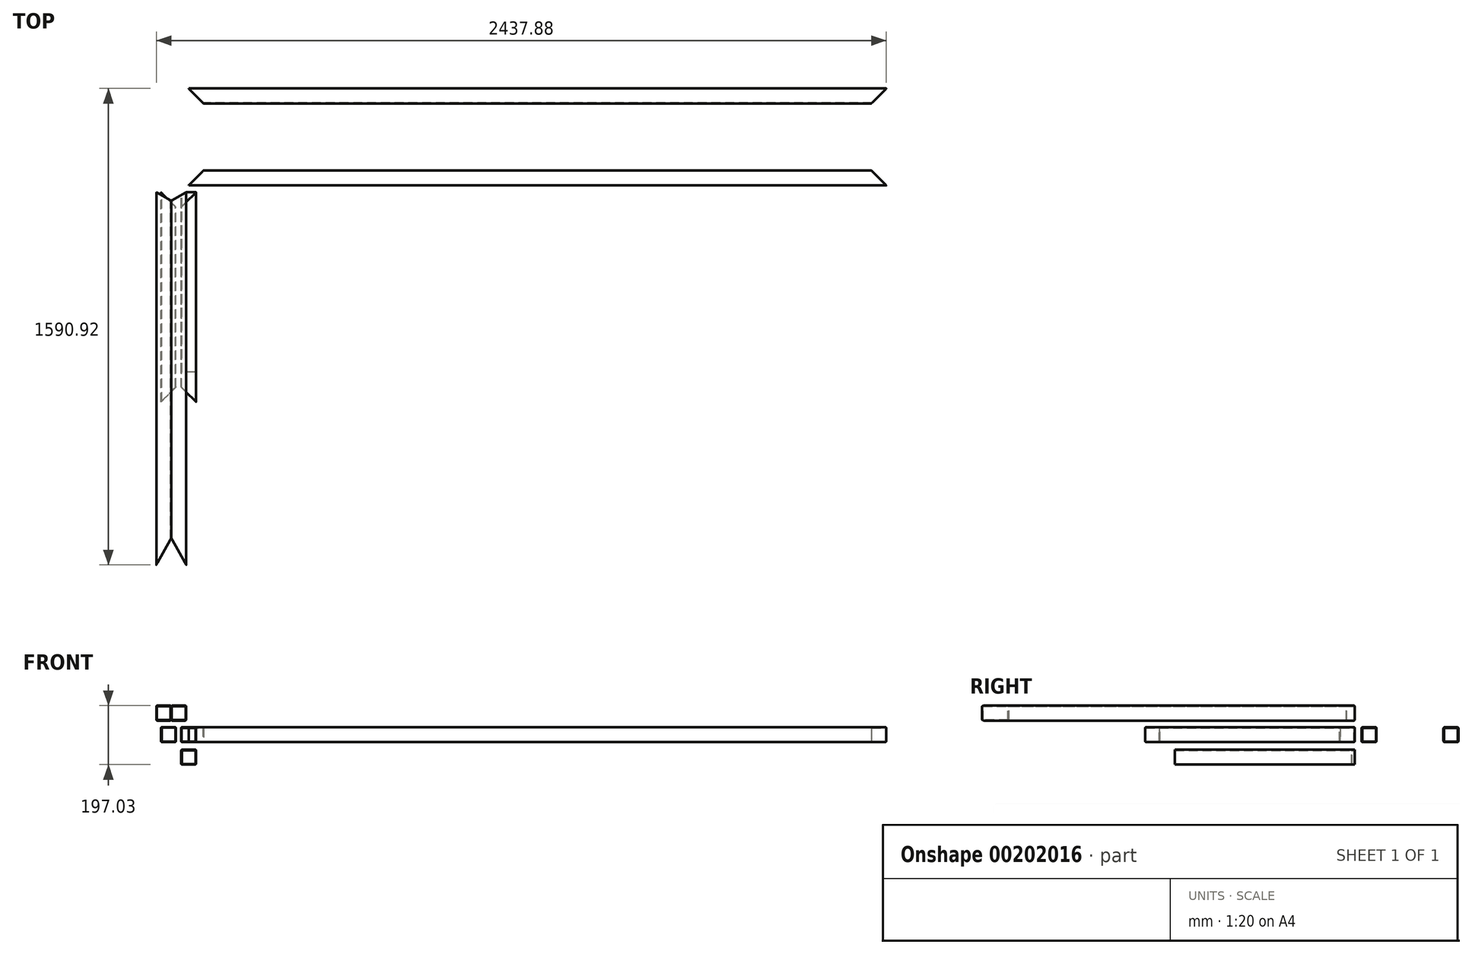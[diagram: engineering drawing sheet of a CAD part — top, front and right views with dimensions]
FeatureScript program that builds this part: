
annotation { "Feature Type Name" : "Feature", "Feature Type Description" : "" }
export const myFeature = defineFeature(function(context is Context, id is Id, definition is map)
    precondition{}
    {
        {
            var Q0;
            Q0=qCreatedBy(makeId("Front.planeOp"),FACE);
            var sketch = newSketch(context, id + "F0", { "sketchPlane" : qUnion([Q0])});
            skLineSegment(sketch, "E0.bottom", {"start": v(21, 25) * mm, "end": v(-21, 25) * mm});
            skLineSegment(sketch, "E0.top", {"start": v(21, -25) * mm, "end": v(-21, -25) * mm});
            skLineSegment(sketch, "E0.left", {"start": v(25, 21) * mm, "end": v(25, -21) * mm});
            skLineSegment(sketch, "E0.right", {"start": v(-25, 21) * mm, "end": v(-25, -21) * mm});
            skPoint(sketch, "E0.middle", {"position": v(0, 0) * mm});
            skPoint(sketch, "E1.visualSharp", {"position": v(-25, 25) * mm});
            skArc(sketch, "E1.filletArc", {"start": v(-21, 25) * mm, "mid": v(-23.83, 23.83) * mm, "end": v(-25, 21) * mm});
            skPoint(sketch, "E2.visualSharp", {"position": v(25, 25) * mm});
            skArc(sketch, "E2.filletArc", {"start": v(25, 21) * mm, "mid": v(23.83, 23.83) * mm, "end": v(21, 25) * mm});
            skPoint(sketch, "E3.visualSharp", {"position": v(25, -25) * mm});
            skArc(sketch, "E3.filletArc", {"start": v(21, -25) * mm, "mid": v(23.83, -23.83) * mm, "end": v(25, -21) * mm});
            skPoint(sketch, "E4.visualSharp", {"position": v(-25, -25) * mm});
            skArc(sketch, "E4.filletArc", {"start": v(-25, -21) * mm, "mid": v(-23.83, -23.83) * mm, "end": v(-21, -25) * mm});
            skLineSegment(sketch, "E5.0", {"start": v(-23, 23) * mm, "end": v(-23, -23) * mm});
            skLineSegment(sketch, "E5.1", {"start": v(23, 23) * mm, "end": v(-23, 23) * mm});
            skLineSegment(sketch, "E5.2", {"start": v(23, 23) * mm, "end": v(23, -23) * mm});
            skLineSegment(sketch, "E5.3", {"start": v(23, -23) * mm, "end": v(-23, -23) * mm});
            skSolve(sketch);
        }
        {
            var Q0;
            Q0=makeQuery(id+"F0.imprint","IMPRINT",FACE,{"disambiguationData":[TD([[makeQuery(id+"F0.imprint","IMPRINT",EDGE,{"derivedFrom":sQuery(id+"F0.wireOp",EDGE,"E0.bottom")}),1.0]])]});
            extrude(context, id + "F1", {"entities" : qUnion([Q0]), "depth" : 700 * mm});
        }
        {
            var Q0;
            Q0=qCreatedBy(makeId("Front.planeOp"),FACE);
            var sketch = newSketch(context, id + "F2", { "sketchPlane" : qUnion([Q0])});
            skLineSegment(sketch, "E6.bottom", {"start": v(-46.1, 25.24) * mm, "end": v(-88.1, 25.24) * mm});
            skLineSegment(sketch, "E6.top", {"start": v(-46.1, -24.76) * mm, "end": v(-88.1, -24.76) * mm});
            skLineSegment(sketch, "E6.left", {"start": v(-42.1, 21.24) * mm, "end": v(-42.1, -20.76) * mm});
            skLineSegment(sketch, "E6.right", {"start": v(-92.1, 21.24) * mm, "end": v(-92.1, -20.76) * mm});
            skPoint(sketch, "E6.middle", {"position": v(-67.1, 0.24) * mm});
            skPoint(sketch, "E7.visualSharp", {"position": v(-92.1, 25.24) * mm});
            skArc(sketch, "E7.filletArc", {"start": v(-88.1, 25.24) * mm, "mid": v(-90.93, 24.07) * mm, "end": v(-92.1, 21.24) * mm});
            skPoint(sketch, "E8.visualSharp", {"position": v(-42.1, 25.24) * mm});
            skArc(sketch, "E8.filletArc", {"start": v(-42.1, 21.24) * mm, "mid": v(-43.28, 24.07) * mm, "end": v(-46.1, 25.24) * mm});
            skPoint(sketch, "E9.visualSharp", {"position": v(-42.1, -24.76) * mm});
            skArc(sketch, "E9.filletArc", {"start": v(-46.1, -24.76) * mm, "mid": v(-43.28, -23.59) * mm, "end": v(-42.1, -20.76) * mm});
            skPoint(sketch, "E10.visualSharp", {"position": v(-92.1, -24.76) * mm});
            skArc(sketch, "E10.filletArc", {"start": v(-92.1, -20.76) * mm, "mid": v(-90.93, -23.59) * mm, "end": v(-88.1, -24.76) * mm});
            skLineSegment(sketch, "E11.0", {"start": v(-90.1, 23.24) * mm, "end": v(-90.1, -22.76) * mm});
            skLineSegment(sketch, "E11.1", {"start": v(-44.1, 23.24) * mm, "end": v(-90.1, 23.24) * mm});
            skLineSegment(sketch, "E11.2", {"start": v(-44.1, 23.24) * mm, "end": v(-44.1, -22.76) * mm});
            skLineSegment(sketch, "E11.3", {"start": v(-44.1, -22.76) * mm, "end": v(-90.1, -22.76) * mm});
            skSolve(sketch);
        }
        {
            var Q0;
            Q0=makeQuery(id+"F2.imprint","IMPRINT",FACE,{"disambiguationData":[TD([[makeQuery(id+"F2.imprint","IMPRINT",EDGE,{"derivedFrom":sQuery(id+"F2.wireOp",EDGE,"E6.bottom")}),1.0]])]});
            extrude(context, id + "F3", {"entities" : qUnion([Q0]), "depth" : 700 * mm});
        }
        {
            var Q0;
            Q0=makeQuery(id+"F1.opExtrude","SWEPT_FACE",FACE,{"disambiguationData":[OSD([sQuery(id+"F0.wireOp",EDGE,"E0.bottom")])]});
            var sketch = newSketch(context, id + "F4", { "sketchPlane" : qUnion([Q0])});
            skLineSegment(sketch, "E12.0", {"start": v(-25, -700) * mm, "end": v(-25, 0) * mm});
            skLineSegment(sketch, "E13.0", {"start": v(25, -700) * mm, "end": v(25, 0) * mm});
            skLineSegment(sketch, "E14", {"start": v(25, 0) * mm, "end": v(-25, -50) * mm});
            skLineSegment(sketch, "E15", {"start": v(25, -700) * mm, "end": v(-25, -650) * mm});
            skLineSegment(sketch, "E16", {"start": v(25, -700) * mm, "end": v(-25, -700) * mm});
            skLineSegment(sketch, "E17", {"start": v(25, 0) * mm, "end": v(-25, 0) * mm});
            skSolve(sketch);
        }
        {
            var Q0;
            {var subQ0=sQuery(id+"F4.wireOp",EDGE,"E17");var subQ1=sQuery(id+"F4.wireOp",EDGE,"E12.0");var subQ2=makeQuery(id+"F4.imprint","INTERSECT",VERTEX,{"derivedFrom":[subQ1,subQ0]});Q0=makeQuery(id+"F4.imprint","IMPRINT",FACE,{"disambiguationData":[TD([[makeQuery(id+"F4.imprint","IMPRINT",EDGE,{"disambiguationData":[TD([[subQ2,1.0]])],"derivedFrom":subQ1}),-1.0]])]});}
            var Q1;
            {var subQ0=sQuery(id+"F4.wireOp",EDGE,"E14");var subQ1=sQuery(id+"F0.wireOp",EDGE,"E0.bottom");var subQ2=makeQuery(id+"F1.opExtrude","SWEPT_EDGE",EDGE,{"disambiguationData":[OSD([subQ1,sQuery(id+"F0.wireOp",EDGE,"E2.filletArc")])]});var subQ3=makeQuery(id+"F4.imprint","INTERSECT",VERTEX,{"derivedFrom":[subQ2,subQ0]});Q1=makeQuery(id+"F4.imprint","IMPRINT",FACE,{"disambiguationData":[TD([[makeQuery(id+"F4.imprint","IMPRINT",EDGE,{"disambiguationData":[TD([[subQ3,-1.0]])],"derivedFrom":subQ0}),-1.0]])]});}
            var Q2;
            {var subQ0=sQuery(id+"F4.wireOp",EDGE,"E17");var subQ1=sQuery(id+"F4.wireOp",EDGE,"E14");var subQ2=makeQuery(id+"F4.imprint","INTERSECT",VERTEX,{"derivedFrom":[sQuery(id+"F4.wireOp",EDGE,"E13.0"),subQ1,subQ0]});Q2=makeQuery(id+"F4.imprint","IMPRINT",FACE,{"disambiguationData":[TD([[makeQuery(id+"F4.imprint","IMPRINT",EDGE,{"disambiguationData":[TD([[subQ2,-1.0]])],"derivedFrom":subQ1}),-1.0]])]});}
            var Q3;
            {var subQ0=sQuery(id+"F4.wireOp",EDGE,"E16");var subQ1=sQuery(id+"F4.wireOp",EDGE,"E12.0");var subQ2=makeQuery(id+"F4.imprint","INTERSECT",VERTEX,{"derivedFrom":[subQ1,subQ0]});Q3=makeQuery(id+"F4.imprint","IMPRINT",FACE,{"disambiguationData":[TD([[makeQuery(id+"F4.imprint","IMPRINT",EDGE,{"disambiguationData":[TD([[subQ2,-1.0]])],"derivedFrom":subQ1}),-1.0]])]});}
            var Q4;
            {var subQ0=sQuery(id+"F4.wireOp",EDGE,"E15");var subQ1=sQuery(id+"F0.wireOp",EDGE,"E0.bottom");var subQ2=makeQuery(id+"F1.opExtrude","SWEPT_EDGE",EDGE,{"disambiguationData":[OSD([subQ1,sQuery(id+"F0.wireOp",EDGE,"E2.filletArc")])]});var subQ3=makeQuery(id+"F4.imprint","INTERSECT",VERTEX,{"derivedFrom":[subQ2,subQ0]});Q4=makeQuery(id+"F4.imprint","IMPRINT",FACE,{"disambiguationData":[TD([[makeQuery(id+"F4.imprint","IMPRINT",EDGE,{"disambiguationData":[TD([[subQ3,-1.0]])],"derivedFrom":subQ0}),1.0]])]});}
            var Q5;
            {var subQ0=sQuery(id+"F4.wireOp",EDGE,"E16");var subQ1=sQuery(id+"F4.wireOp",EDGE,"E15");var subQ2=makeQuery(id+"F4.imprint","INTERSECT",VERTEX,{"derivedFrom":[sQuery(id+"F4.wireOp",EDGE,"E13.0"),subQ1,subQ0]});Q5=makeQuery(id+"F4.imprint","IMPRINT",FACE,{"disambiguationData":[TD([[makeQuery(id+"F4.imprint","IMPRINT",EDGE,{"disambiguationData":[TD([[subQ2,-1.0]])],"derivedFrom":subQ1}),1.0]])]});}
            extrude(context, id + "F5", {"entities" : qUnion([Q0, Q1, Q2, Q3, Q4, Q5]), "operationType" : NewBodyOperationType.REMOVE, "endBound" : BoundingType.THROUGH_ALL, "oppositeDirection" : true, "depth" : 25 * mm});
        }
        {
            var Q0;
            Q0=makeQuery(id+"F3.opExtrude","SWEPT_FACE",FACE,{"disambiguationData":[OSD([sQuery(id+"F2.wireOp",EDGE,"E6.bottom")])]});
            var sketch = newSketch(context, id + "F6", { "sketchPlane" : qUnion([Q0])});
            skLineSegment(sketch, "E18.0", {"start": v(-92.1, -700) * mm, "end": v(-92.1, 0) * mm});
            skLineSegment(sketch, "E19.0", {"start": v(-42.1, -700) * mm, "end": v(-42.1, 0) * mm});
            skLineSegment(sketch, "E20", {"start": v(-92.1, -700) * mm, "end": v(-42.1, -700) * mm});
            skLineSegment(sketch, "E21", {"start": v(-92.1, -700) * mm, "end": v(-42.1, -650) * mm});
            skLineSegment(sketch, "E22", {"start": v(-42.1, 0) * mm, "end": v(-92.1, 0) * mm});
            skLineSegment(sketch, "E23", {"start": v(-92.1, 0) * mm, "end": v(-42.1, -50) * mm});
            skSolve(sketch);
        }
        {
            var Q0;
            {var subQ0=sQuery(id+"F6.wireOp",EDGE,"E22");var subQ1=makeQuery(id+"F3.opExtrude","SWEPT_EDGE",EDGE,{"disambiguationData":[OSD([sQuery(id+"F2.wireOp",EDGE,"E6.bottom"),sQuery(id+"F2.wireOp",EDGE,"E7.filletArc")])]});var subQ2=makeQuery(id+"F6.imprint","INTERSECT",VERTEX,{"derivedFrom":[subQ1,subQ0]});Q0=makeQuery(id+"F6.imprint","IMPRINT",FACE,{"disambiguationData":[TD([[makeQuery(id+"F6.imprint","IMPRINT",EDGE,{"disambiguationData":[TD([[subQ2,-1.0]])],"derivedFrom":subQ0}),1.0]])]});}
            var Q1;
            {var subQ0=sQuery(id+"F6.wireOp",EDGE,"E22");var subQ1=sQuery(id+"F2.wireOp",EDGE,"E6.bottom");var subQ2=makeQuery(id+"F3.opExtrude","SWEPT_EDGE",EDGE,{"disambiguationData":[OSD([subQ1,sQuery(id+"F2.wireOp",EDGE,"E8.filletArc")])]});var subQ3=makeQuery(id+"F6.imprint","INTERSECT",VERTEX,{"derivedFrom":[subQ2,subQ0]});Q1=makeQuery(id+"F6.imprint","IMPRINT",FACE,{"disambiguationData":[TD([[makeQuery(id+"F6.imprint","IMPRINT",EDGE,{"disambiguationData":[TD([[subQ3,-1.0]])],"derivedFrom":subQ0}),1.0]])]});}
            var Q2;
            {var subQ0=sQuery(id+"F6.wireOp",EDGE,"E22");var subQ1=sQuery(id+"F6.wireOp",EDGE,"E19.0");var subQ2=makeQuery(id+"F6.imprint","INTERSECT",VERTEX,{"derivedFrom":[subQ1,subQ0]});Q2=makeQuery(id+"F6.imprint","IMPRINT",FACE,{"disambiguationData":[TD([[makeQuery(id+"F6.imprint","IMPRINT",EDGE,{"disambiguationData":[TD([[subQ2,1.0]])],"derivedFrom":subQ1}),1.0]])]});}
            var Q3;
            {var subQ0=sQuery(id+"F6.wireOp",EDGE,"E20");var subQ1=sQuery(id+"F6.wireOp",EDGE,"E19.0");var subQ2=makeQuery(id+"F6.imprint","INTERSECT",VERTEX,{"derivedFrom":[subQ1,subQ0]});Q3=makeQuery(id+"F6.imprint","IMPRINT",FACE,{"disambiguationData":[TD([[makeQuery(id+"F6.imprint","IMPRINT",EDGE,{"disambiguationData":[TD([[subQ2,-1.0]])],"derivedFrom":subQ1}),1.0]])]});}
            var Q4;
            {var subQ0=sQuery(id+"F6.wireOp",EDGE,"E20");var subQ1=sQuery(id+"F2.wireOp",EDGE,"E6.bottom");var subQ2=makeQuery(id+"F3.opExtrude","SWEPT_EDGE",EDGE,{"disambiguationData":[OSD([subQ1,sQuery(id+"F2.wireOp",EDGE,"E8.filletArc")])]});var subQ3=makeQuery(id+"F6.imprint","INTERSECT",VERTEX,{"derivedFrom":[subQ2,subQ0]});var subQ4=makeQuery(id+"F3.opExtrude","SWEPT_EDGE",EDGE,{"disambiguationData":[OSD([subQ1,sQuery(id+"F2.wireOp",EDGE,"E7.filletArc")])]});var subQ5=makeQuery(id+"F6.imprint","INTERSECT",VERTEX,{"derivedFrom":[subQ4,subQ0]});Q4=makeQuery(id+"F6.imprint","IMPRINT",FACE,{"disambiguationData":[TD([[makeQuery(id+"F6.imprint","IMPRINT",EDGE,{"disambiguationData":[TD([[subQ3,-1.0],[subQ5,1.0]])],"derivedFrom":subQ0}),-1.0]])]});}
            var Q5;
            {var subQ0=sQuery(id+"F6.wireOp",EDGE,"E20");var subQ1=makeQuery(id+"F3.opExtrude","SWEPT_EDGE",EDGE,{"disambiguationData":[OSD([sQuery(id+"F2.wireOp",EDGE,"E6.bottom"),sQuery(id+"F2.wireOp",EDGE,"E7.filletArc")])]});var subQ2=makeQuery(id+"F6.imprint","INTERSECT",VERTEX,{"derivedFrom":[subQ1,subQ0]});var subQ3=sQuery(id+"F6.wireOp",EDGE,"E21");var subQ4=makeQuery(id+"F6.imprint","INTERSECT",VERTEX,{"derivedFrom":[sQuery(id+"F6.wireOp",EDGE,"E18.0"),subQ0,subQ3]});Q5=makeQuery(id+"F6.imprint","IMPRINT",FACE,{"disambiguationData":[TD([[makeQuery(id+"F6.imprint","IMPRINT",EDGE,{"disambiguationData":[TD([[subQ2,1.0],[subQ4,-1.0]])],"derivedFrom":subQ0}),1.0]])]});}
            extrude(context, id + "F7", {"entities" : qUnion([Q0, Q1, Q2, Q3, Q4, Q5]), "operationType" : NewBodyOperationType.REMOVE, "endBound" : BoundingType.THROUGH_ALL, "oppositeDirection" : true, "depth" : 25 * mm});
        }
        {
            var Q0;
            Q0=qCreatedBy(makeId("Right.planeOp"),FACE);
            var sketch = newSketch(context, id + "F8", { "sketchPlane" : qUnion([Q0])});
            skLineSegment(sketch, "E24.bottom", {"start": v(342.69, -25) * mm, "end": v(300.69, -25) * mm});
            skLineSegment(sketch, "E24.top", {"start": v(342.69, 25) * mm, "end": v(300.69, 25) * mm});
            skLineSegment(sketch, "E24.left", {"start": v(346.69, -21) * mm, "end": v(346.69, 21) * mm});
            skLineSegment(sketch, "E24.right", {"start": v(296.69, -21) * mm, "end": v(296.69, 21) * mm});
            skPoint(sketch, "E24.middle", {"position": v(321.69, 0) * mm});
            skPoint(sketch, "E25.visualSharp", {"position": v(346.69, -25) * mm});
            skArc(sketch, "E25.filletArc", {"start": v(342.69, -25) * mm, "mid": v(345.52, -23.83) * mm, "end": v(346.69, -21) * mm});
            skPoint(sketch, "E26.visualSharp", {"position": v(296.69, -25) * mm});
            skArc(sketch, "E26.filletArc", {"start": v(296.69, -21) * mm, "mid": v(297.86, -23.83) * mm, "end": v(300.69, -25) * mm});
            skPoint(sketch, "E27.visualSharp", {"position": v(296.69, 25) * mm});
            skArc(sketch, "E27.filletArc", {"start": v(300.69, 25) * mm, "mid": v(297.86, 23.83) * mm, "end": v(296.69, 21) * mm});
            skPoint(sketch, "E28.visualSharp", {"position": v(346.69, 25) * mm});
            skArc(sketch, "E28.filletArc", {"start": v(346.69, 21) * mm, "mid": v(345.52, 23.83) * mm, "end": v(342.69, 25) * mm});
            skLineSegment(sketch, "E29.0", {"start": v(298.69, -23) * mm, "end": v(298.69, 23) * mm});
            skLineSegment(sketch, "E29.1", {"start": v(344.69, -23) * mm, "end": v(298.69, -23) * mm});
            skLineSegment(sketch, "E29.2", {"start": v(344.69, -23) * mm, "end": v(344.69, 23) * mm});
            skLineSegment(sketch, "E29.3", {"start": v(344.69, 23) * mm, "end": v(298.69, 23) * mm});
            skSolve(sketch);
        }
        {
            var Q0;
            Q0=qCreatedBy(makeId("Right.planeOp"),FACE);
            var sketch = newSketch(context, id + "F9", { "sketchPlane" : qUnion([Q0])});
            skLineSegment(sketch, "E30.bottom", {"start": v(69.15, -25) * mm, "end": v(27.15, -25) * mm});
            skLineSegment(sketch, "E30.top", {"start": v(69.15, 25) * mm, "end": v(27.15, 25) * mm});
            skLineSegment(sketch, "E30.left", {"start": v(73.15, -21) * mm, "end": v(73.15, 21) * mm});
            skLineSegment(sketch, "E30.right", {"start": v(23.15, -21) * mm, "end": v(23.15, 21) * mm});
            skPoint(sketch, "E30.middle", {"position": v(48.15, 0) * mm});
            skPoint(sketch, "E31.visualSharp", {"position": v(73.15, -25) * mm});
            skArc(sketch, "E31.filletArc", {"start": v(69.15, -25) * mm, "mid": v(71.98, -23.83) * mm, "end": v(73.15, -21) * mm});
            skPoint(sketch, "E32.visualSharp", {"position": v(23.15, -25) * mm});
            skArc(sketch, "E32.filletArc", {"start": v(23.15, -21) * mm, "mid": v(24.32, -23.83) * mm, "end": v(27.15, -25) * mm});
            skPoint(sketch, "E33.visualSharp", {"position": v(23.15, 25) * mm});
            skArc(sketch, "E33.filletArc", {"start": v(27.15, 25) * mm, "mid": v(24.32, 23.83) * mm, "end": v(23.15, 21) * mm});
            skPoint(sketch, "E34.visualSharp", {"position": v(73.15, 25) * mm});
            skArc(sketch, "E34.filletArc", {"start": v(73.15, 21) * mm, "mid": v(71.98, 23.83) * mm, "end": v(69.15, 25) * mm});
            skLineSegment(sketch, "E35.0", {"start": v(25.15, -23) * mm, "end": v(25.15, 23) * mm});
            skLineSegment(sketch, "E35.1", {"start": v(71.15, -23) * mm, "end": v(25.15, -23) * mm});
            skLineSegment(sketch, "E35.2", {"start": v(71.15, -23) * mm, "end": v(71.15, 23) * mm});
            skLineSegment(sketch, "E35.3", {"start": v(71.15, 23) * mm, "end": v(25.15, 23) * mm});
            skSolve(sketch);
        }
        {
            var Q0;
            Q0=makeQuery(id+"F8.imprint","IMPRINT",FACE,{"disambiguationData":[TD([[makeQuery(id+"F8.imprint","IMPRINT",EDGE,{"derivedFrom":sQuery(id+"F8.wireOp",EDGE,"E24.bottom")}),-1.0]])]});
            extrude(context, id + "F10", {"entities" : qUnion([Q0]), "depth" : 2330 * mm});
        }
        {
            var Q0;
            Q0=makeQuery(id+"F9.imprint","IMPRINT",FACE,{"disambiguationData":[TD([[makeQuery(id+"F9.imprint","IMPRINT",EDGE,{"derivedFrom":sQuery(id+"F9.wireOp",EDGE,"E30.bottom")}),-1.0]])]});
            extrude(context, id + "F11", {"entities" : qUnion([Q0]), "depth" : 2330 * mm});
        }
        {
            var Q0;
            Q0=makeQuery(id+"F11.opExtrude","SWEPT_FACE",FACE,{"disambiguationData":[OSD([sQuery(id+"F9.wireOp",EDGE,"E30.bottom")])]});
            var sketch = newSketch(context, id + "F12", { "sketchPlane" : qUnion([Q0])});
            skLineSegment(sketch, "E36.0", {"start": v(2330, -73.15) * mm, "end": v(0, -73.15) * mm});
            skLineSegment(sketch, "E37.0", {"start": v(2330, -23.15) * mm, "end": v(0, -23.15) * mm});
            skLineSegment(sketch, "E38", {"start": v(0, -73.15) * mm, "end": v(0, -23.15) * mm});
            skLineSegment(sketch, "E39", {"start": v(0, -23.15) * mm, "end": v(50, -73.15) * mm});
            skLineSegment(sketch, "E40", {"start": v(2330, -73.15) * mm, "end": v(2330, -23.15) * mm});
            skLineSegment(sketch, "E41", {"start": v(2280, -73.15) * mm, "end": v(2330, -23.15) * mm});
            skSolve(sketch);
        }
        {
            var Q0;
            {var subQ0=sQuery(id+"F12.wireOp",EDGE,"E40");var subQ1=sQuery(id+"F12.wireOp",EDGE,"E36.0");var subQ2=makeQuery(id+"F12.imprint","INTERSECT",VERTEX,{"derivedFrom":[subQ1,subQ0]});Q0=makeQuery(id+"F12.imprint","IMPRINT",FACE,{"disambiguationData":[TD([[makeQuery(id+"F12.imprint","IMPRINT",EDGE,{"disambiguationData":[TD([[subQ2,-1.0]])],"derivedFrom":subQ1}),-1.0]])]});}
            var Q1;
            {var subQ0=sQuery(id+"F12.wireOp",EDGE,"E40");var subQ1=sQuery(id+"F9.wireOp",EDGE,"E30.bottom");var subQ2=makeQuery(id+"F11.opExtrude","SWEPT_EDGE",EDGE,{"disambiguationData":[OSD([subQ1,sQuery(id+"F9.wireOp",EDGE,"E31.filletArc")])]});var subQ3=makeQuery(id+"F12.imprint","INTERSECT",VERTEX,{"derivedFrom":[subQ2,subQ0]});Q1=makeQuery(id+"F12.imprint","IMPRINT",FACE,{"disambiguationData":[TD([[makeQuery(id+"F12.imprint","IMPRINT",EDGE,{"disambiguationData":[TD([[subQ3,-1.0]])],"derivedFrom":subQ0}),1.0]])]});}
            var Q2;
            {var subQ0=sQuery(id+"F12.wireOp",EDGE,"E40");var subQ1=makeQuery(id+"F11.opExtrude","SWEPT_EDGE",EDGE,{"disambiguationData":[OSD([sQuery(id+"F9.wireOp",EDGE,"E30.bottom"),sQuery(id+"F9.wireOp",EDGE,"E32.filletArc")])]});var subQ2=makeQuery(id+"F12.imprint","INTERSECT",VERTEX,{"derivedFrom":[subQ1,subQ0]});Q2=makeQuery(id+"F12.imprint","IMPRINT",FACE,{"disambiguationData":[TD([[makeQuery(id+"F12.imprint","IMPRINT",EDGE,{"disambiguationData":[TD([[subQ2,-1.0]])],"derivedFrom":subQ0}),1.0]])]});}
            var Q3;
            {var subQ0=sQuery(id+"F12.wireOp",EDGE,"E38");var subQ1=sQuery(id+"F12.wireOp",EDGE,"E36.0");var subQ2=makeQuery(id+"F12.imprint","INTERSECT",VERTEX,{"derivedFrom":[subQ1,subQ0]});Q3=makeQuery(id+"F12.imprint","IMPRINT",FACE,{"disambiguationData":[TD([[makeQuery(id+"F12.imprint","IMPRINT",EDGE,{"disambiguationData":[TD([[subQ2,1.0]])],"derivedFrom":subQ1}),-1.0]])]});}
            var Q4;
            {var subQ0=sQuery(id+"F12.wireOp",EDGE,"E38");var subQ1=sQuery(id+"F9.wireOp",EDGE,"E30.bottom");var subQ2=makeQuery(id+"F11.opExtrude","SWEPT_EDGE",EDGE,{"disambiguationData":[OSD([subQ1,sQuery(id+"F9.wireOp",EDGE,"E31.filletArc")])]});var subQ3=makeQuery(id+"F12.imprint","INTERSECT",VERTEX,{"derivedFrom":[subQ2,subQ0]});Q4=makeQuery(id+"F12.imprint","IMPRINT",FACE,{"disambiguationData":[TD([[makeQuery(id+"F12.imprint","IMPRINT",EDGE,{"disambiguationData":[TD([[subQ3,-1.0]])],"derivedFrom":subQ0}),-1.0]])]});}
            var Q5;
            {var subQ0=sQuery(id+"F12.wireOp",EDGE,"E38");var subQ1=makeQuery(id+"F11.opExtrude","SWEPT_EDGE",EDGE,{"disambiguationData":[OSD([sQuery(id+"F9.wireOp",EDGE,"E30.bottom"),sQuery(id+"F9.wireOp",EDGE,"E32.filletArc")])]});var subQ2=makeQuery(id+"F12.imprint","INTERSECT",VERTEX,{"derivedFrom":[subQ1,subQ0]});Q5=makeQuery(id+"F12.imprint","IMPRINT",FACE,{"disambiguationData":[TD([[makeQuery(id+"F12.imprint","IMPRINT",EDGE,{"disambiguationData":[TD([[subQ2,-1.0]])],"derivedFrom":subQ0}),-1.0]])]});}
            extrude(context, id + "F13", {"entities" : qUnion([Q0, Q1, Q2, Q3, Q4, Q5]), "operationType" : NewBodyOperationType.REMOVE, "endBound" : BoundingType.THROUGH_ALL, "oppositeDirection" : true, "depth" : 25 * mm});
        }
        {
            var Q0;
            Q0=makeQuery(id+"F10.opExtrude","SWEPT_FACE",FACE,{"disambiguationData":[OSD([sQuery(id+"F8.wireOp",EDGE,"E24.bottom")])]});
            var sketch = newSketch(context, id + "F14", { "sketchPlane" : qUnion([Q0])});
            skLineSegment(sketch, "E42.0", {"start": v(2330, -346.69) * mm, "end": v(0, -346.69) * mm});
            skLineSegment(sketch, "E43.0", {"start": v(2330, -296.69) * mm, "end": v(0, -296.69) * mm});
            skLineSegment(sketch, "E44", {"start": v(0, -296.69) * mm, "end": v(0, -346.69) * mm});
            skLineSegment(sketch, "E45", {"start": v(50, -296.69) * mm, "end": v(0, -346.69) * mm});
            skLineSegment(sketch, "E46", {"start": v(2330, -296.69) * mm, "end": v(2330, -346.69) * mm});
            skLineSegment(sketch, "E47", {"start": v(2330, -346.69) * mm, "end": v(2280, -296.69) * mm});
            skSolve(sketch);
        }
        {
            var Q0;
            {var subQ0=sQuery(id+"F14.wireOp",EDGE,"E46");var subQ1=makeQuery(id+"F10.opExtrude","SWEPT_EDGE",EDGE,{"disambiguationData":[OSD([sQuery(id+"F8.wireOp",EDGE,"E24.bottom"),sQuery(id+"F8.wireOp",EDGE,"E25.filletArc")])]});var subQ2=makeQuery(id+"F14.imprint","INTERSECT",VERTEX,{"derivedFrom":[subQ1,subQ0]});var subQ3=sQuery(id+"F14.wireOp",EDGE,"E47");var subQ4=makeQuery(id+"F14.imprint","INTERSECT",VERTEX,{"derivedFrom":[sQuery(id+"F14.wireOp",EDGE,"E42.0"),subQ0,subQ3]});Q0=makeQuery(id+"F14.imprint","IMPRINT",FACE,{"disambiguationData":[TD([[makeQuery(id+"F14.imprint","IMPRINT",EDGE,{"disambiguationData":[TD([[subQ2,-1.0],[subQ4,1.0]])],"derivedFrom":subQ0}),-1.0]])]});}
            var Q1;
            {var subQ0=sQuery(id+"F14.wireOp",EDGE,"E46");var subQ1=sQuery(id+"F8.wireOp",EDGE,"E24.bottom");var subQ2=makeQuery(id+"F10.opExtrude","SWEPT_EDGE",EDGE,{"disambiguationData":[OSD([subQ1,sQuery(id+"F8.wireOp",EDGE,"E25.filletArc")])]});var subQ3=makeQuery(id+"F14.imprint","INTERSECT",VERTEX,{"derivedFrom":[subQ2,subQ0]});var subQ4=makeQuery(id+"F10.opExtrude","SWEPT_EDGE",EDGE,{"disambiguationData":[OSD([subQ1,sQuery(id+"F8.wireOp",EDGE,"E26.filletArc")])]});var subQ5=makeQuery(id+"F14.imprint","INTERSECT",VERTEX,{"derivedFrom":[subQ4,subQ0]});Q1=makeQuery(id+"F14.imprint","IMPRINT",FACE,{"disambiguationData":[TD([[makeQuery(id+"F14.imprint","IMPRINT",EDGE,{"disambiguationData":[TD([[subQ3,-1.0],[subQ5,1.0]])],"derivedFrom":subQ0}),1.0]])]});}
            var Q2;
            {var subQ0=sQuery(id+"F14.wireOp",EDGE,"E46");var subQ1=sQuery(id+"F14.wireOp",EDGE,"E43.0");var subQ2=makeQuery(id+"F14.imprint","INTERSECT",VERTEX,{"derivedFrom":[subQ1,subQ0]});Q2=makeQuery(id+"F14.imprint","IMPRINT",FACE,{"disambiguationData":[TD([[makeQuery(id+"F14.imprint","IMPRINT",EDGE,{"disambiguationData":[TD([[subQ2,-1.0]])],"derivedFrom":subQ1}),1.0]])]});}
            var Q3;
            {var subQ0=sQuery(id+"F14.wireOp",EDGE,"E44");var subQ1=sQuery(id+"F14.wireOp",EDGE,"E43.0");var subQ2=makeQuery(id+"F14.imprint","INTERSECT",VERTEX,{"derivedFrom":[subQ1,subQ0]});Q3=makeQuery(id+"F14.imprint","IMPRINT",FACE,{"disambiguationData":[TD([[makeQuery(id+"F14.imprint","IMPRINT",EDGE,{"disambiguationData":[TD([[subQ2,1.0]])],"derivedFrom":subQ1}),1.0]])]});}
            var Q4;
            {var subQ0=sQuery(id+"F14.wireOp",EDGE,"E44");var subQ1=sQuery(id+"F8.wireOp",EDGE,"E24.bottom");var subQ2=makeQuery(id+"F10.opExtrude","SWEPT_EDGE",EDGE,{"disambiguationData":[OSD([subQ1,sQuery(id+"F8.wireOp",EDGE,"E25.filletArc")])]});var subQ3=makeQuery(id+"F14.imprint","INTERSECT",VERTEX,{"derivedFrom":[subQ2,subQ0]});var subQ4=makeQuery(id+"F10.opExtrude","SWEPT_EDGE",EDGE,{"disambiguationData":[OSD([subQ1,sQuery(id+"F8.wireOp",EDGE,"E26.filletArc")])]});var subQ5=makeQuery(id+"F14.imprint","INTERSECT",VERTEX,{"derivedFrom":[subQ4,subQ0]});Q4=makeQuery(id+"F14.imprint","IMPRINT",FACE,{"disambiguationData":[TD([[makeQuery(id+"F14.imprint","IMPRINT",EDGE,{"disambiguationData":[TD([[subQ3,-1.0],[subQ5,1.0]])],"derivedFrom":subQ0}),-1.0]])]});}
            var Q5;
            {var subQ0=sQuery(id+"F14.wireOp",EDGE,"E44");var subQ1=makeQuery(id+"F10.opExtrude","SWEPT_EDGE",EDGE,{"disambiguationData":[OSD([sQuery(id+"F8.wireOp",EDGE,"E24.bottom"),sQuery(id+"F8.wireOp",EDGE,"E25.filletArc")])]});var subQ2=makeQuery(id+"F14.imprint","INTERSECT",VERTEX,{"derivedFrom":[subQ1,subQ0]});var subQ3=sQuery(id+"F14.wireOp",EDGE,"E45");var subQ4=makeQuery(id+"F14.imprint","INTERSECT",VERTEX,{"derivedFrom":[sQuery(id+"F14.wireOp",EDGE,"E42.0"),subQ0,subQ3]});Q5=makeQuery(id+"F14.imprint","IMPRINT",FACE,{"disambiguationData":[TD([[makeQuery(id+"F14.imprint","IMPRINT",EDGE,{"disambiguationData":[TD([[subQ2,-1.0],[subQ4,1.0]])],"derivedFrom":subQ0}),1.0]])]});}
            extrude(context, id + "F15", {"entities" : qUnion([Q0, Q1, Q2, Q3, Q4, Q5]), "operationType" : NewBodyOperationType.REMOVE, "endBound" : BoundingType.THROUGH_ALL, "oppositeDirection" : true, "depth" : 25 * mm});
        }
        {
            var Q0;
            Q0=qCreatedBy(makeId("Front.planeOp"),FACE);
            var sketch = newSketch(context, id + "F16", { "sketchPlane" : qUnion([Q0])});
            skLineSegment(sketch, "E48.bottom", {"start": v(21.25, -49.95) * mm, "end": v(-20.75, -49.95) * mm});
            skLineSegment(sketch, "E48.top", {"start": v(21.25, -99.95) * mm, "end": v(-20.75, -99.95) * mm});
            skLineSegment(sketch, "E48.left", {"start": v(25.25, -53.95) * mm, "end": v(25.25, -95.95) * mm});
            skLineSegment(sketch, "E48.right", {"start": v(-24.75, -53.95) * mm, "end": v(-24.75, -95.95) * mm});
            skPoint(sketch, "E48.middle", {"position": v(0.25, -74.95) * mm});
            skPoint(sketch, "E49.visualSharp", {"position": v(-24.75, -49.95) * mm});
            skArc(sketch, "E49.filletArc", {"start": v(-20.75, -49.95) * mm, "mid": v(-23.58, -51.13) * mm, "end": v(-24.75, -53.95) * mm});
            skPoint(sketch, "E50.visualSharp", {"position": v(25.25, -49.95) * mm});
            skArc(sketch, "E50.filletArc", {"start": v(25.25, -53.95) * mm, "mid": v(24.08, -51.13) * mm, "end": v(21.25, -49.95) * mm});
            skPoint(sketch, "E51.visualSharp", {"position": v(25.25, -99.95) * mm});
            skArc(sketch, "E51.filletArc", {"start": v(21.25, -99.95) * mm, "mid": v(24.08, -98.78) * mm, "end": v(25.25, -95.95) * mm});
            skPoint(sketch, "E52.visualSharp", {"position": v(-24.75, -99.95) * mm});
            skArc(sketch, "E52.filletArc", {"start": v(-24.75, -95.95) * mm, "mid": v(-23.58, -98.78) * mm, "end": v(-20.75, -99.95) * mm});
            skLineSegment(sketch, "E53.0", {"start": v(-22.75, -51.95) * mm, "end": v(-22.75, -97.95) * mm});
            skLineSegment(sketch, "E53.1", {"start": v(23.25, -51.95) * mm, "end": v(-22.75, -51.95) * mm});
            skLineSegment(sketch, "E53.2", {"start": v(23.25, -51.95) * mm, "end": v(23.25, -97.95) * mm});
            skLineSegment(sketch, "E53.3", {"start": v(23.25, -97.95) * mm, "end": v(-22.75, -97.95) * mm});
            skSolve(sketch);
        }
        {
            var Q0;
            Q0=makeQuery(id+"F16.imprint","IMPRINT",FACE,{"disambiguationData":[TD([[makeQuery(id+"F16.imprint","IMPRINT",EDGE,{"derivedFrom":sQuery(id+"F16.wireOp",EDGE,"E48.bottom")}),1.0]])]});
            extrude(context, id + "F17", {"entities" : qUnion([Q0]), "depth" : 600 * mm});
        }
        {
            var Q0;
            Q0=qCreatedBy(makeId("Front.planeOp"),FACE);
            var sketch = newSketch(context, id + "F18", { "sketchPlane" : qUnion([Q0])});
            skLineSegment(sketch, "E54.bottom", {"start": v(60.67, 97.08) * mm, "end": v(18.67, 97.08) * mm});
            skLineSegment(sketch, "E54.top", {"start": v(60.67, 47.08) * mm, "end": v(18.67, 47.08) * mm});
            skLineSegment(sketch, "E54.left", {"start": v(64.67, 93.08) * mm, "end": v(64.67, 51.08) * mm});
            skLineSegment(sketch, "E54.right", {"start": v(14.67, 93.08) * mm, "end": v(14.67, 51.08) * mm});
            skPoint(sketch, "E54.middle", {"position": v(39.67, 72.08) * mm});
            skPoint(sketch, "E55.visualSharp", {"position": v(14.67, 97.08) * mm});
            skArc(sketch, "E55.filletArc", {"start": v(18.67, 97.08) * mm, "mid": v(15.84, 95.91) * mm, "end": v(14.67, 93.08) * mm});
            skPoint(sketch, "E56.visualSharp", {"position": v(64.67, 97.08) * mm});
            skArc(sketch, "E56.filletArc", {"start": v(64.67, 93.08) * mm, "mid": v(63.5, 95.91) * mm, "end": v(60.67, 97.08) * mm});
            skPoint(sketch, "E57.visualSharp", {"position": v(64.67, 47.08) * mm});
            skArc(sketch, "E57.filletArc", {"start": v(60.67, 47.08) * mm, "mid": v(63.5, 48.25) * mm, "end": v(64.67, 51.08) * mm});
            skPoint(sketch, "E58.visualSharp", {"position": v(14.67, 47.08) * mm});
            skArc(sketch, "E58.filletArc", {"start": v(14.67, 51.08) * mm, "mid": v(15.84, 48.25) * mm, "end": v(18.67, 47.08) * mm});
            skLineSegment(sketch, "E59.0", {"start": v(16.67, 95.08) * mm, "end": v(16.67, 49.08) * mm});
            skLineSegment(sketch, "E59.1", {"start": v(62.67, 95.08) * mm, "end": v(16.67, 95.08) * mm});
            skLineSegment(sketch, "E59.2", {"start": v(62.67, 95.08) * mm, "end": v(62.67, 49.08) * mm});
            skLineSegment(sketch, "E59.3", {"start": v(62.67, 49.08) * mm, "end": v(16.67, 49.08) * mm});
            skSolve(sketch);
        }
        {
            var Q0;
            Q0=qCreatedBy(makeId("Front.planeOp"),FACE);
            var sketch = newSketch(context, id + "F19", { "sketchPlane" : qUnion([Q0])});
            skLineSegment(sketch, "E60.bottom", {"start": v(-11.88, 97.08) * mm, "end": v(-53.88, 97.08) * mm});
            skLineSegment(sketch, "E60.top", {"start": v(-11.88, 47.08) * mm, "end": v(-53.88, 47.08) * mm});
            skLineSegment(sketch, "E60.left", {"start": v(-7.88, 93.08) * mm, "end": v(-7.88, 51.08) * mm});
            skLineSegment(sketch, "E60.right", {"start": v(-57.88, 93.08) * mm, "end": v(-57.88, 51.08) * mm});
            skPoint(sketch, "E60.middle", {"position": v(-32.88, 72.08) * mm});
            skPoint(sketch, "E61.visualSharp", {"position": v(-57.88, 97.08) * mm});
            skArc(sketch, "E61.filletArc", {"start": v(-53.88, 97.08) * mm, "mid": v(-56.7, 95.91) * mm, "end": v(-57.88, 93.08) * mm});
            skPoint(sketch, "E62.visualSharp", {"position": v(-7.88, 97.08) * mm});
            skArc(sketch, "E62.filletArc", {"start": v(-7.88, 93.08) * mm, "mid": v(-9.05, 95.91) * mm, "end": v(-11.88, 97.08) * mm});
            skPoint(sketch, "E63.visualSharp", {"position": v(-7.88, 47.08) * mm});
            skArc(sketch, "E63.filletArc", {"start": v(-11.88, 47.08) * mm, "mid": v(-9.05, 48.25) * mm, "end": v(-7.88, 51.08) * mm});
            skPoint(sketch, "E64.visualSharp", {"position": v(-57.88, 47.08) * mm});
            skArc(sketch, "E64.filletArc", {"start": v(-57.88, 51.08) * mm, "mid": v(-56.7, 48.25) * mm, "end": v(-53.88, 47.08) * mm});
            skLineSegment(sketch, "E65.0", {"start": v(-55.88, 95.08) * mm, "end": v(-55.88, 49.08) * mm});
            skLineSegment(sketch, "E65.1", {"start": v(-9.88, 95.08) * mm, "end": v(-55.88, 95.08) * mm});
            skLineSegment(sketch, "E65.2", {"start": v(-9.88, 95.08) * mm, "end": v(-9.88, 49.08) * mm});
            skLineSegment(sketch, "E65.3", {"start": v(-9.88, 49.08) * mm, "end": v(-55.88, 49.08) * mm});
            skSolve(sketch);
        }
        {
            var Q0;
            Q0=makeQuery(id+"F18.imprint","IMPRINT",FACE,{"disambiguationData":[TD([[makeQuery(id+"F18.imprint","IMPRINT",EDGE,{"derivedFrom":sQuery(id+"F18.wireOp",EDGE,"E54.bottom")}),1.0]])]});
            extrude(context, id + "F20", {"entities" : qUnion([Q0]), "depth" : 1244.23 * mm});
        }
        {
            var Q0;
            Q0=makeQuery(id+"F19.imprint","IMPRINT",FACE,{"disambiguationData":[TD([[makeQuery(id+"F19.imprint","IMPRINT",EDGE,{"derivedFrom":sQuery(id+"F19.wireOp",EDGE,"E60.bottom")}),1.0]])]});
            extrude(context, id + "F21", {"entities" : qUnion([Q0]), "depth" : 1244.23 * mm});
        }
        {
            var Q0;
            Q0=makeQuery(id+"F21.opExtrude","SWEPT_FACE",FACE,{"disambiguationData":[OSD([sQuery(id+"F19.wireOp",EDGE,"E60.bottom")])]});
            var sketch = newSketch(context, id + "F22", { "sketchPlane" : qUnion([Q0])});
            skLineSegment(sketch, "E66.0", {"start": v(-57.88, -1244.23) * mm, "end": v(-57.88, 0) * mm});
            skLineSegment(sketch, "E67.0", {"start": v(-7.88, -1244.23) * mm, "end": v(-7.88, 0) * mm});
            skLineSegment(sketch, "E68", {"start": v(-57.88, 0) * mm, "end": v(-7.88, 0) * mm});
            skLineSegment(sketch, "E69", {"start": v(-7.88, 0) * mm, "end": v(-57.88, -27.72) * mm});
            skLineSegment(sketch, "E70", {"start": v(-57.88, -1244.23) * mm, "end": v(-7.88, -1244.23) * mm});
            skLineSegment(sketch, "E71", {"start": v(-7.88, -1244.23) * mm, "end": v(-57.88, -1154.02) * mm});
            skSolve(sketch);
        }
        {
            var Q0;
            {var subQ0=sQuery(id+"F22.wireOp",EDGE,"E70");var subQ1=sQuery(id+"F22.wireOp",EDGE,"E66.0");var subQ2=makeQuery(id+"F22.imprint","INTERSECT",VERTEX,{"derivedFrom":[subQ1,subQ0]});Q0=makeQuery(id+"F22.imprint","IMPRINT",FACE,{"disambiguationData":[TD([[makeQuery(id+"F22.imprint","IMPRINT",EDGE,{"disambiguationData":[TD([[subQ2,-1.0]])],"derivedFrom":subQ1}),-1.0]])]});}
            var Q1;
            {var subQ0=sQuery(id+"F22.wireOp",EDGE,"E70");var subQ1=sQuery(id+"F19.wireOp",EDGE,"E60.bottom");var subQ2=makeQuery(id+"F21.opExtrude","SWEPT_EDGE",EDGE,{"disambiguationData":[OSD([subQ1,sQuery(id+"F19.wireOp",EDGE,"E62.filletArc")])]});var subQ3=makeQuery(id+"F22.imprint","INTERSECT",VERTEX,{"derivedFrom":[subQ2,subQ0]});var subQ4=makeQuery(id+"F21.opExtrude","SWEPT_EDGE",EDGE,{"disambiguationData":[OSD([subQ1,sQuery(id+"F19.wireOp",EDGE,"E61.filletArc")])]});var subQ5=makeQuery(id+"F22.imprint","INTERSECT",VERTEX,{"derivedFrom":[subQ4,subQ0]});Q1=makeQuery(id+"F22.imprint","IMPRINT",FACE,{"disambiguationData":[TD([[makeQuery(id+"F22.imprint","IMPRINT",EDGE,{"disambiguationData":[TD([[subQ3,-1.0],[subQ5,1.0]])],"derivedFrom":subQ0}),-1.0]])]});}
            var Q2;
            {var subQ0=sQuery(id+"F22.wireOp",EDGE,"E70");var subQ1=makeQuery(id+"F21.opExtrude","SWEPT_EDGE",EDGE,{"disambiguationData":[OSD([sQuery(id+"F19.wireOp",EDGE,"E60.bottom"),sQuery(id+"F19.wireOp",EDGE,"E62.filletArc")])]});var subQ2=makeQuery(id+"F22.imprint","INTERSECT",VERTEX,{"derivedFrom":[subQ1,subQ0]});var subQ3=sQuery(id+"F22.wireOp",EDGE,"E71");var subQ4=makeQuery(id+"F22.imprint","INTERSECT",VERTEX,{"derivedFrom":[sQuery(id+"F22.wireOp",EDGE,"E67.0"),subQ0,subQ3]});Q2=makeQuery(id+"F22.imprint","IMPRINT",FACE,{"disambiguationData":[TD([[makeQuery(id+"F22.imprint","IMPRINT",EDGE,{"disambiguationData":[TD([[subQ2,-1.0],[subQ4,1.0]])],"derivedFrom":subQ0}),1.0]])]});}
            var Q3;
            {var subQ0=sQuery(id+"F22.wireOp",EDGE,"E68");var subQ1=sQuery(id+"F22.wireOp",EDGE,"E66.0");var subQ2=makeQuery(id+"F22.imprint","INTERSECT",VERTEX,{"derivedFrom":[subQ1,subQ0]});Q3=makeQuery(id+"F22.imprint","IMPRINT",FACE,{"disambiguationData":[TD([[makeQuery(id+"F22.imprint","IMPRINT",EDGE,{"disambiguationData":[TD([[subQ2,1.0]])],"derivedFrom":subQ1}),-1.0]])]});}
            var Q4;
            {var subQ0=sQuery(id+"F22.wireOp",EDGE,"E68");var subQ1=sQuery(id+"F19.wireOp",EDGE,"E60.bottom");var subQ2=makeQuery(id+"F21.opExtrude","SWEPT_EDGE",EDGE,{"disambiguationData":[OSD([subQ1,sQuery(id+"F19.wireOp",EDGE,"E62.filletArc")])]});var subQ3=makeQuery(id+"F22.imprint","INTERSECT",VERTEX,{"derivedFrom":[subQ2,subQ0]});var subQ4=makeQuery(id+"F21.opExtrude","SWEPT_EDGE",EDGE,{"disambiguationData":[OSD([subQ1,sQuery(id+"F19.wireOp",EDGE,"E61.filletArc")])]});var subQ5=makeQuery(id+"F22.imprint","INTERSECT",VERTEX,{"derivedFrom":[subQ4,subQ0]});Q4=makeQuery(id+"F22.imprint","IMPRINT",FACE,{"disambiguationData":[TD([[makeQuery(id+"F22.imprint","IMPRINT",EDGE,{"disambiguationData":[TD([[subQ3,-1.0],[subQ5,1.0]])],"derivedFrom":subQ0}),1.0]])]});}
            var Q5;
            {var subQ0=sQuery(id+"F22.wireOp",EDGE,"E68");var subQ1=makeQuery(id+"F21.opExtrude","SWEPT_EDGE",EDGE,{"disambiguationData":[OSD([sQuery(id+"F19.wireOp",EDGE,"E60.bottom"),sQuery(id+"F19.wireOp",EDGE,"E62.filletArc")])]});var subQ2=makeQuery(id+"F22.imprint","INTERSECT",VERTEX,{"derivedFrom":[subQ1,subQ0]});var subQ3=sQuery(id+"F22.wireOp",EDGE,"E69");var subQ4=makeQuery(id+"F22.imprint","INTERSECT",VERTEX,{"derivedFrom":[sQuery(id+"F22.wireOp",EDGE,"E67.0"),subQ0,subQ3]});Q5=makeQuery(id+"F22.imprint","IMPRINT",FACE,{"disambiguationData":[TD([[makeQuery(id+"F22.imprint","IMPRINT",EDGE,{"disambiguationData":[TD([[subQ2,-1.0],[subQ4,1.0]])],"derivedFrom":subQ0}),-1.0]])]});}
            extrude(context, id + "F23", {"entities" : qUnion([Q0, Q1, Q2, Q3, Q4, Q5]), "operationType" : NewBodyOperationType.REMOVE, "endBound" : BoundingType.THROUGH_ALL, "oppositeDirection" : true, "depth" : 25 * mm});
        }
        {
            var Q0;
            Q0=makeQuery(id+"F21.opExtrude","SWEPT_BODY",BODY,{"disambiguationData":[OSD([sQuery(id+"F19.wireOp",EDGE,"E60.bottom"),sQuery(id+"F19.wireOp",EDGE,"E60.top"),sQuery(id+"F19.wireOp",EDGE,"E60.left"),sQuery(id+"F19.wireOp",EDGE,"E60.right"),sQuery(id+"F19.wireOp",EDGE,"E61.filletArc"),sQuery(id+"F19.wireOp",EDGE,"E62.filletArc"),sQuery(id+"F19.wireOp",EDGE,"E63.filletArc"),sQuery(id+"F19.wireOp",EDGE,"E64.filletArc"),sQuery(id+"F19.wireOp",EDGE,"E65.0"),sQuery(id+"F19.wireOp",EDGE,"E65.1"),sQuery(id+"F19.wireOp",EDGE,"E65.2"),sQuery(id+"F19.wireOp",EDGE,"E65.3")])]});
            var Q1;
            Q1=makeQuery(id+"F21.opExtrude","SWEPT_FACE",FACE,{"disambiguationData":[OSD([sQuery(id+"F19.wireOp",EDGE,"E60.right")])]});
            mirror(context, id + "F24", {"entities" : qUnion([Q0]), "mirrorPlane" : qUnion([Q1])});
        }
        {
            var Q0;
            Q0=makeQuery(id+"F20.opExtrude","SWEPT_BODY",BODY,{"disambiguationData":[OSD([sQuery(id+"F18.wireOp",EDGE,"E54.bottom"),sQuery(id+"F18.wireOp",EDGE,"E54.top"),sQuery(id+"F18.wireOp",EDGE,"E54.left"),sQuery(id+"F18.wireOp",EDGE,"E54.right"),sQuery(id+"F18.wireOp",EDGE,"E55.filletArc"),sQuery(id+"F18.wireOp",EDGE,"E56.filletArc"),sQuery(id+"F18.wireOp",EDGE,"E57.filletArc"),sQuery(id+"F18.wireOp",EDGE,"E58.filletArc"),sQuery(id+"F18.wireOp",EDGE,"E59.0"),sQuery(id+"F18.wireOp",EDGE,"E59.1"),sQuery(id+"F18.wireOp",EDGE,"E59.2"),sQuery(id+"F18.wireOp",EDGE,"E59.3")])]});
            deleteBodies(context, id + "F25", {"entities" : qUnion([Q0])});
        }
    });
